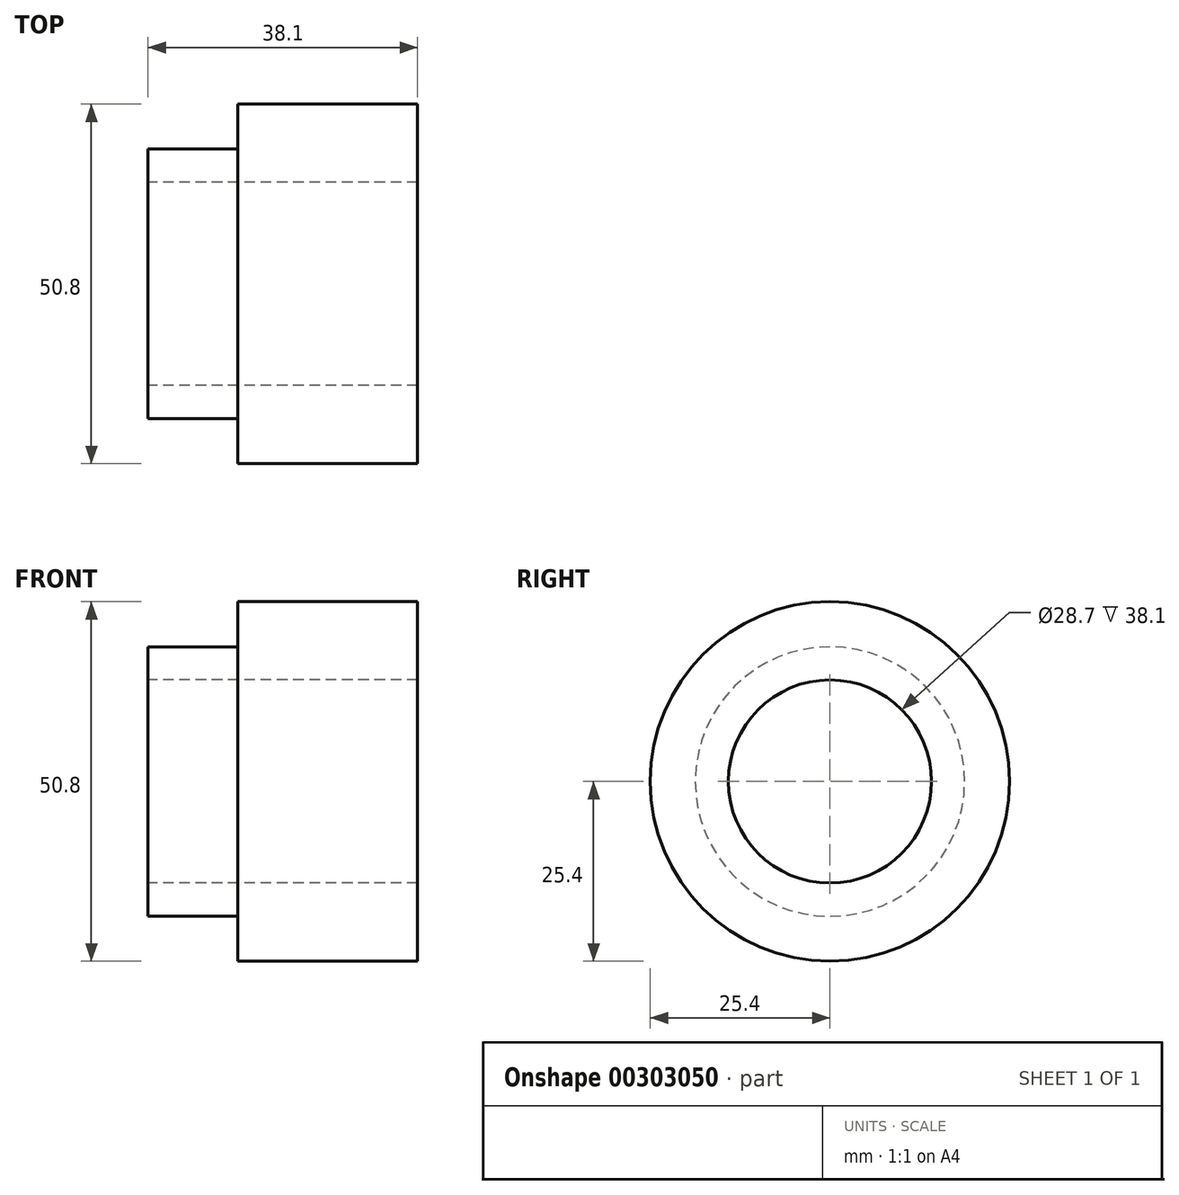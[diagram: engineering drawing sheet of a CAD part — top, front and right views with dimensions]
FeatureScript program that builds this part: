
annotation { "Feature Type Name" : "Feature", "Feature Type Description" : "" }
export const myFeature = defineFeature(function(context is Context, id is Id, definition is map)
    precondition{}
    {
        {
            var Q0;
            Q0=qCreatedBy(makeId("Front.planeOp"),FACE);
            var sketch = newSketch(context, id + "F0", { "sketchPlane" : qUnion([Q0])});
            skLineSegment(sketch, "E0", {"start": v(-19.05, 19.04) * mm, "end": v(-19.05, -19.04) * mm});
            skLineSegment(sketch, "E1", {"start": v(19.05, 25.4) * mm, "end": v(19.05, -25.4) * mm});
            skLineSegment(sketch, "E2", {"start": v(19.05, 25.4) * mm, "end": v(-6.35, 25.4) * mm});
            skLineSegment(sketch, "E3", {"start": v(19.05, -25.4) * mm, "end": v(-6.35, -25.4) * mm});
            skLineSegment(sketch, "E4", {"start": v(-19.05, 19.04) * mm, "end": v(-6.35, 19.04) * mm});
            skLineSegment(sketch, "E5", {"start": v(-6.35, 25.4) * mm, "end": v(-6.35, 19.04) * mm});
            skLineSegment(sketch, "E6", {"start": v(-19.05, -19.04) * mm, "end": v(-6.35, -19.04) * mm});
            skLineSegment(sketch, "E7", {"start": v(-6.35, -19.04) * mm, "end": v(-6.35, -25.4) * mm});
            skLineSegment(sketch, "E8", {"start": v(-19.05, 14.35) * mm, "end": v(19.05, 14.35) * mm});
            skLineSegment(sketch, "E9", {"start": v(-19.05, -14.35) * mm, "end": v(19.05, -14.35) * mm});
            skLineSegment(sketch, "E10", {"start": v(-35.87, 0) * mm, "end": v(41.92, 0) * mm, "construction": true});
            skSolve(sketch);
        }
        {
            var Q0;
            {var subQ1=sQuery(id+"F0.wireOp",EDGE,"E2");Q0=makeQuery(id+"F0.imprint","IMPRINT",FACE,{"disambiguationData":[TD([[makeQuery(id+"F0.imprint","IMPRINT",EDGE,{"derivedFrom":subQ1}),1.0]])]});}
            var Q1;
            Q1=sQuery(id+"F0.wireOp",EDGE,"E10");
            revolve(context, id + "F1", {"entities" : qUnion([Q0]), "axis" : qUnion([Q1]), "revolveType" : RevolveType.FULL});
        }
    });
